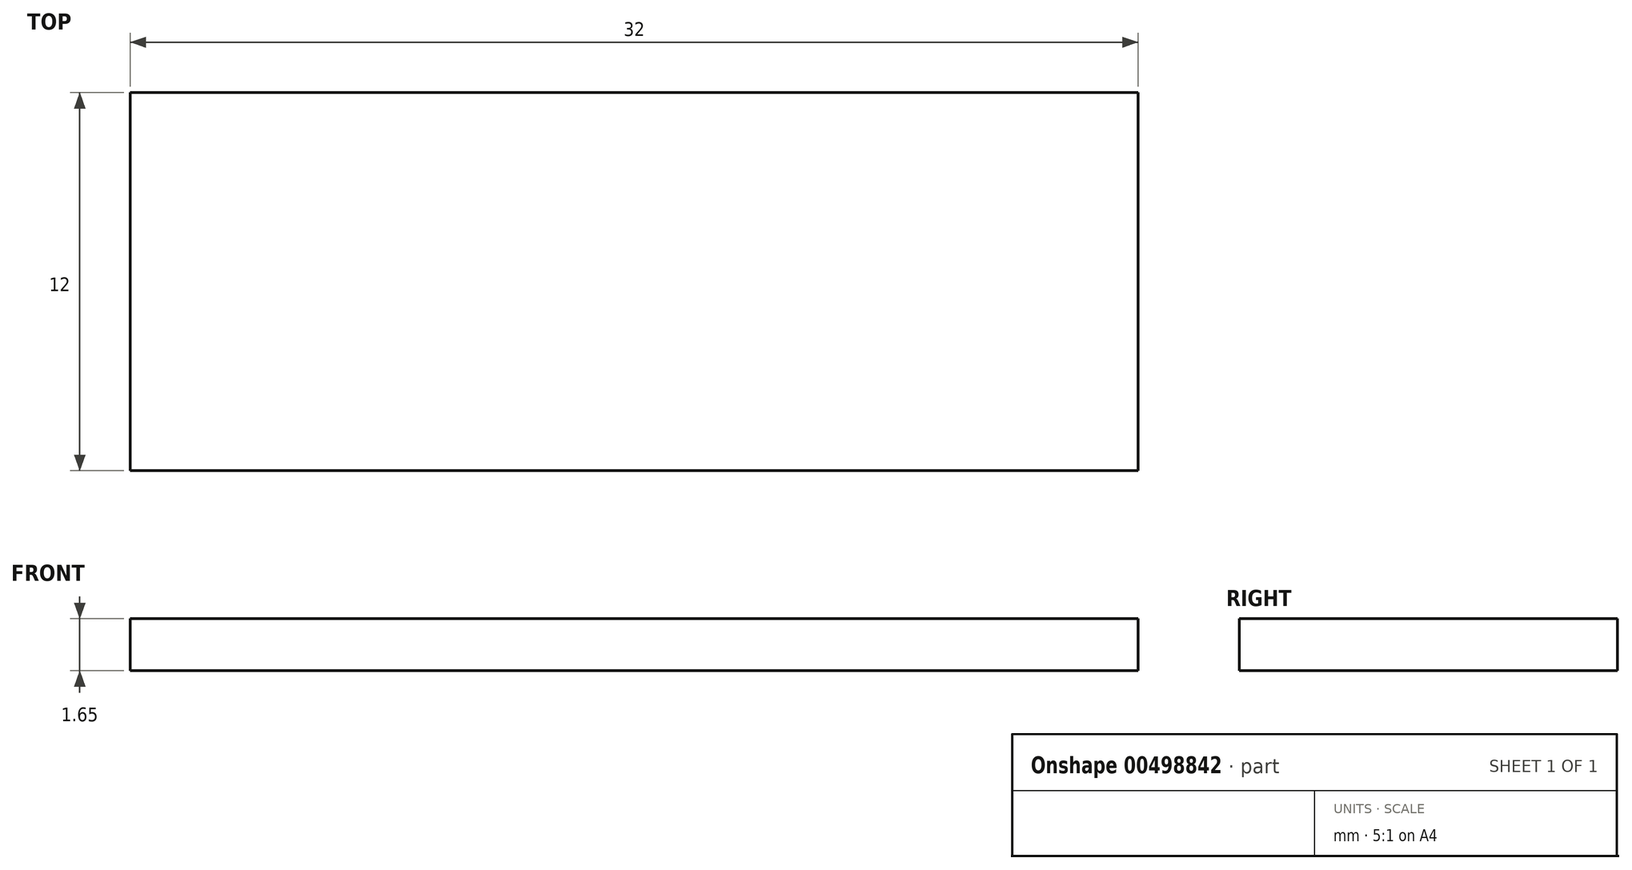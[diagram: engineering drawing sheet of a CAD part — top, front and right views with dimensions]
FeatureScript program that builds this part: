
annotation { "Feature Type Name" : "Feature", "Feature Type Description" : "" }
export const myFeature = defineFeature(function(context is Context, id is Id, definition is map)
    precondition{}
    {
        {
            var Q0;
            Q0=qCreatedBy(makeId("Top.planeOp"),FACE);
            var sketch = newSketch(context, id + "F0", { "sketchPlane" : qUnion([Q0])});
            skLineSegment(sketch, "E0.bottom", {"start": v(-29.65, 9.16) * mm, "end": v(2.35, 9.16) * mm});
            skLineSegment(sketch, "E0.top", {"start": v(-29.65, -2.84) * mm, "end": v(2.35, -2.84) * mm});
            skLineSegment(sketch, "E0.left", {"start": v(-29.65, 9.16) * mm, "end": v(-29.65, -2.84) * mm});
            skLineSegment(sketch, "E0.right", {"start": v(2.35, 9.16) * mm, "end": v(2.35, -2.84) * mm});
            skSolve(sketch);
        }
        {
            var Q0;
            Q0 = qSketchRegion(id + "F0", true);
            extrude(context, id + "F1", {"entities" : qUnion([Q0]), "depth" : 1.65 * mm});
        }
    });
